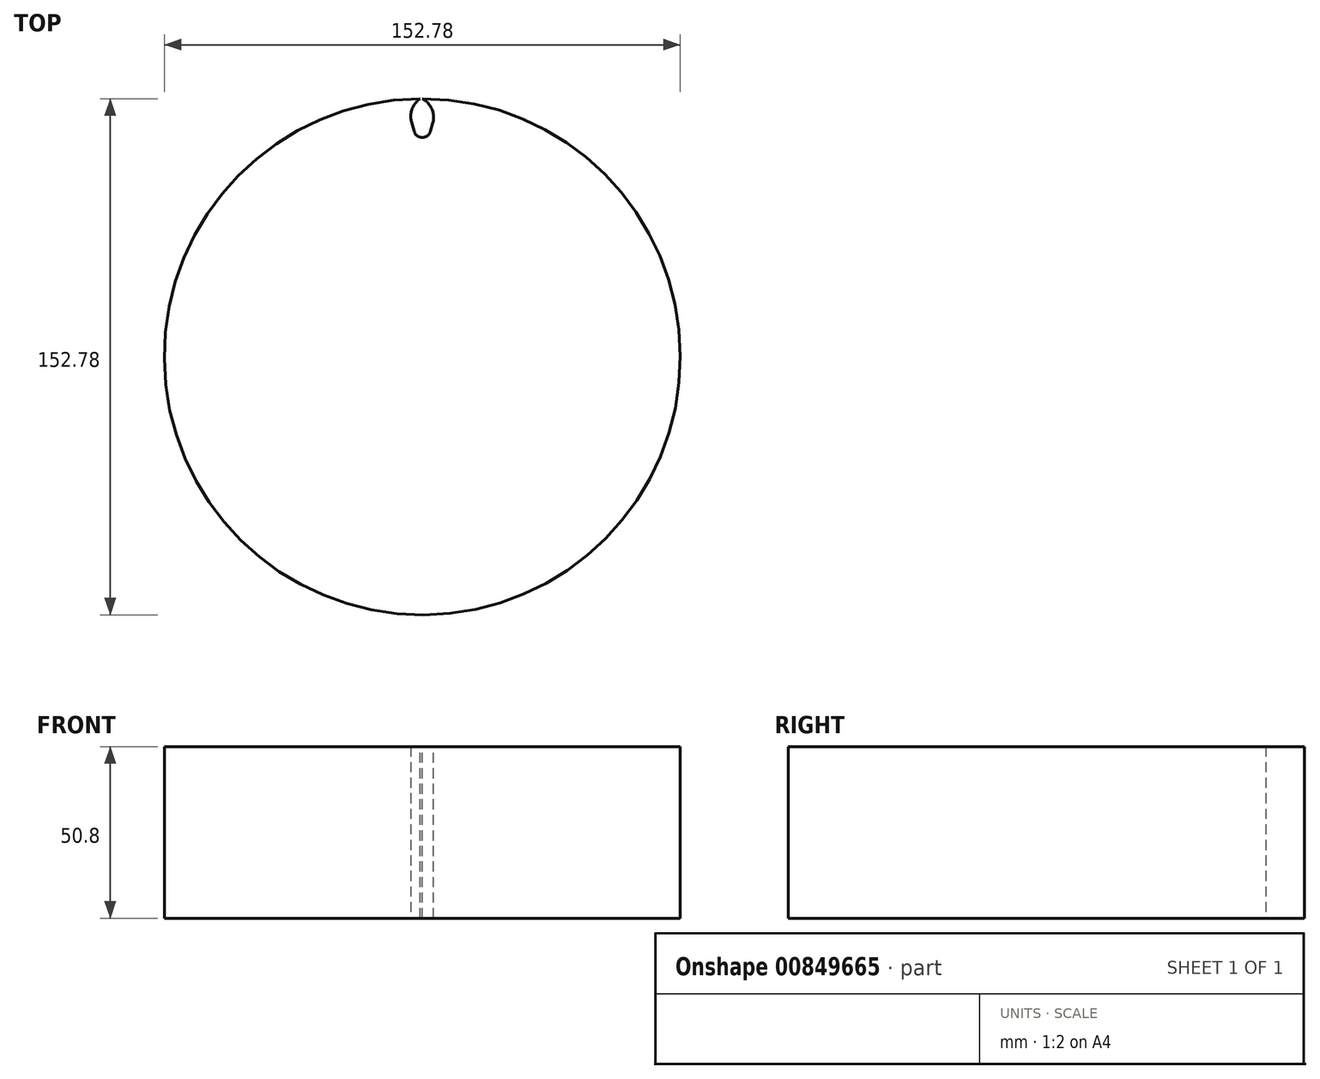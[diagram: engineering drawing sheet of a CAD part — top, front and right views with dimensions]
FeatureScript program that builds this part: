
annotation { "Feature Type Name" : "Feature", "Feature Type Description" : "" }
export const myFeature = defineFeature(function(context is Context, id is Id, definition is map)
    precondition{}
    {
        {
            var Q0;
            Q0=qCreatedBy(makeId("Top.planeOp"),FACE);
            var sketch = newSketch(context, id + "F0", { "sketchPlane" : qUnion([Q0])});
            skCircle(sketch, "E0", {"center": v(0, 0) * mm, "radius": 76.39 * mm});
            skSolve(sketch);
        }
        {
            var Q0;
            Q0=makeQuery(id+"F0.imprint","IMPRINT",FACE,{"disambiguationData":[TD([[makeQuery(id+"F0.imprint","IMPRINT",EDGE,{"derivedFrom":sQuery(id+"F0.wireOp",EDGE,"E0")}),1.0]])]});
            extrude(context, id + "F1", {"entities" : qUnion([Q0]), "depth" : 25.4 * mm, "offsetDistance" : 25.4 * mm});
        }
        {
            var Q0;
            Q0=makeQuery(id+"F1.opExtrude","CAP_FACE",FACE,{"disambiguationData":[OSD([sQuery(id+"F0.wireOp",EDGE,"E0")])],"isStart":false});
            extrude(context, id + "F2", {"entities" : qUnion([Q0]), "operationType" : NewBodyOperationType.ADD, "depth" : 25.4 * mm, "offsetDistance" : 25.4 * mm});
        }
        {
            var Q0;
            Q0=makeQuery(id+"F2.opExtrude","CAP_FACE",FACE,{"disambiguationData":[OSD([sQuery(id+"F0.wireOp",EDGE,"E0")])],"isStart":false});
            var sketch = newSketch(context, id + "F3", { "sketchPlane" : qUnion([Q0])});
            skLineSegment(sketch, "E1", {"start": v(0, 0) * mm, "end": v(10.63, 75.65) * mm, "construction": true});
            skLineSegment(sketch, "E2", {"start": v(10.63, 75.65) * mm, "end": v(-10.63, 75.65) * mm, "construction": true});
            skLineSegment(sketch, "E3", {"start": v(-10.63, 75.65) * mm, "end": v(0, 0) * mm, "construction": true});
            skCircle(sketch, "E4", {"center": v(-9.74, 69.3) * mm, "radius": 6.35 * mm, "construction": true});
            skCircle(sketch, "E5", {"center": v(9.75, 69.36) * mm, "radius": 6.35 * mm, "construction": true});
            skLineSegment(sketch, "E6", {"start": v(-5.06, 76.22) * mm, "end": v(0, 57.87) * mm});
            skLineSegment(sketch, "E7", {"start": v(0, 57.87) * mm, "end": v(5.05, 76.22) * mm});
            skArc(sketch, "E8", {"start": v(5.05, 76.22) * mm, "mid": v(0, 76.39) * mm, "end": v(-5.06, 76.22) * mm});
            skSolve(sketch);
        }
        {
            var Q0;
            Q0=makeQuery(id+"F3.imprint","IMPRINT",FACE,{"disambiguationData":[TD([[makeQuery(id+"F3.imprint","IMPRINT",EDGE,{"derivedFrom":sQuery(id+"F3.wireOp",EDGE,"E6")}),1.0]])]});
            extrude(context, id + "F4", {"entities" : qUnion([Q0]), "operationType" : NewBodyOperationType.REMOVE, "oppositeDirection" : true, "depth" : 50.8 * mm, "offsetDistance" : 25.4 * mm});
        }
        {
            var Q0;
            Q0=makeQuery(id+"F4.boolean.opBoolean","COPY",EDGE,{"derivedFrom":makeQuery(id+"F4.opExtrude","SWEPT_EDGE",EDGE,{"disambiguationData":[OSD([sQuery(id+"F0.wireOp",EDGE,"E0"),sQuery(id+"F3.wireOp",EDGE,"E6"),sQuery(id+"F3.wireOp",EDGE,"E8")])]})});
            var Q1;
            Q1=makeQuery(id+"F4.boolean.opBoolean","COPY",EDGE,{"derivedFrom":makeQuery(id+"F4.opExtrude","SWEPT_EDGE",EDGE,{"disambiguationData":[OSD([sQuery(id+"F0.wireOp",EDGE,"E0"),sQuery(id+"F3.wireOp",EDGE,"E7"),sQuery(id+"F3.wireOp",EDGE,"E8")])]})});
            fillet(context, id + "F5", {"entities" : qUnion([Q0, Q1]), "radius" : 6.35 * mm, "tangentPropagation" : true, "allowEdgeOverflow" : false});
        }
        {
            var Q0;
            Q0=makeQuery(id+"F4.boolean.opBoolean","COPY",EDGE,{"derivedFrom":makeQuery(id+"F4.opExtrude","SWEPT_EDGE",EDGE,{"disambiguationData":[OSD([sQuery(id+"F3.wireOp",EDGE,"E6"),sQuery(id+"F3.wireOp",EDGE,"E7")])]})});
            fillet(context, id + "F6", {"entities" : qUnion([Q0]), "radius" : 2.54 * mm, "tangentPropagation" : true, "allowEdgeOverflow" : false});
        }
        {
            var Q0;
            Q0=qCreatedBy(makeId("Right.planeOp"),FACE);
            var sketch = newSketch(context, id + "F7", { "sketchPlane" : qUnion([Q0])});
            skLineSegment(sketch, "E9", {"start": v(0, 0) * mm, "end": v(0, 76.6) * mm, "construction": true});
            skSolve(sketch);
        }
    });
